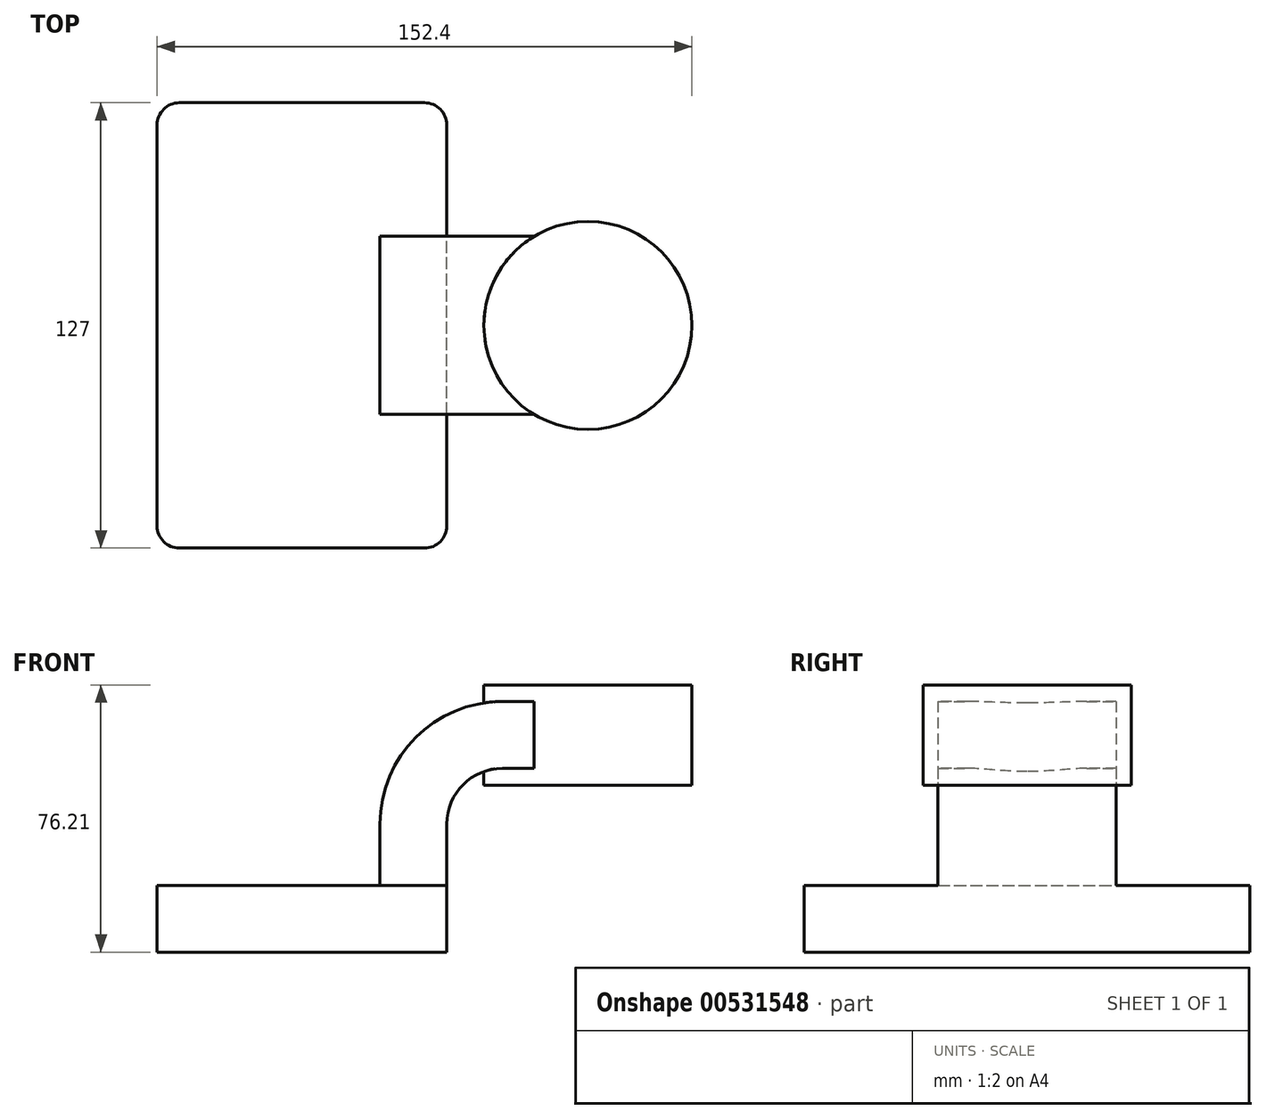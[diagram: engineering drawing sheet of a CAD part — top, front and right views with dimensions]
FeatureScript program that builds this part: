
annotation { "Feature Type Name" : "Feature", "Feature Type Description" : "" }
export const myFeature = defineFeature(function(context is Context, id is Id, definition is map)
    precondition{}
    {
        {
            var Q0;
            Q0=qCreatedBy(makeId("Front.planeOp"),FACE);
            var sketch = newSketch(context, id + "F0", { "sketchPlane" : qUnion([Q0])});
            skLineSegment(sketch, "E0.bottom", {"start": v(-41.28, -9.52) * mm, "end": v(41.28, -9.52) * mm});
            skLineSegment(sketch, "E0.top", {"start": v(-41.28, 9.53) * mm, "end": v(41.28, 9.53) * mm});
            skLineSegment(sketch, "E0.left", {"start": v(-41.28, -9.52) * mm, "end": v(-41.28, 9.53) * mm});
            skLineSegment(sketch, "E0.right", {"start": v(41.28, -9.53) * mm, "end": v(41.28, 9.52) * mm});
            skPoint(sketch, "E0.middle", {"position": v(0, 0) * mm});
            skLineSegment(sketch, "E1.bottom", {"start": v(60.32, 66.68) * mm, "end": v(111.13, 66.68) * mm});
            skLineSegment(sketch, "E1.top", {"start": v(60.32, 38.1) * mm, "end": v(111.13, 38.1) * mm});
            skLineSegment(sketch, "E1.left", {"start": v(60.32, 66.68) * mm, "end": v(60.32, 38.1) * mm});
            skLineSegment(sketch, "E1.right", {"start": v(111.13, 66.68) * mm, "end": v(111.13, 38.1) * mm});
            skPoint(sketch, "E1.middle", {"position": v(85.72, 52.39) * mm});
            skLineSegment(sketch, "E2", {"start": v(41.28, 9.53) * mm, "end": v(41.28, 27) * mm});
            skArc(sketch, "E3", {"start": v(41.28, 27) * mm, "mid": v(45.92, 38.23) * mm, "end": v(57.15, 42.88) * mm});
            skLineSegment(sketch, "E4", {"start": v(57.15, 42.88) * mm, "end": v(81.48, 42.88) * mm});
            skLineSegment(sketch, "E5.0", {"start": v(57.15, 61.93) * mm, "end": v(81.48, 61.93) * mm});
            skArc(sketch, "E5.1", {"start": v(22.23, 27) * mm, "mid": v(32.45, 51.7) * mm, "end": v(57.15, 61.93) * mm});
            skLineSegment(sketch, "E5.2", {"start": v(22.23, 9.52) * mm, "end": v(22.22, 27) * mm});
            skLineSegment(sketch, "E6", {"start": v(81.48, 38.1) * mm, "end": v(81.48, 66.68) * mm});
            skFitSpline(sketch, "E7", {"points": [v(-41.28, 9.53) * mm, v(57.15, 61.93) * mm], "startDerivative": vector(41.68, 78.65) * mm, "endDerivative": vector(125.38, -1.15) * mm});
            skSolve(sketch);
        }
        {
            var Q0;
            Q0=qCreatedBy(makeId("Front.planeOp"),FACE);
            var sketch = newSketch(context, id + "F1", { "sketchPlane" : qUnion([Q0])});
            skLineSegment(sketch, "E8.bottom", {"start": v(-41.28, -9.53) * mm, "end": v(41.28, -9.53) * mm});
            skLineSegment(sketch, "E8.top", {"start": v(-41.28, 9.52) * mm, "end": v(41.28, 9.52) * mm});
            skLineSegment(sketch, "E8.left", {"start": v(-41.28, -9.53) * mm, "end": v(-41.28, 9.52) * mm});
            skLineSegment(sketch, "E8.right", {"start": v(41.28, -9.53) * mm, "end": v(41.28, 9.52) * mm});
            skPoint(sketch, "E8.middle", {"position": v(0, 0) * mm});
            skLineSegment(sketch, "E9.bottom", {"start": v(67.76, 64.92) * mm, "end": v(118.56, 64.92) * mm});
            skLineSegment(sketch, "E9.top", {"start": v(67.76, 36.35) * mm, "end": v(118.56, 36.35) * mm});
            skLineSegment(sketch, "E9.left", {"start": v(67.76, 64.92) * mm, "end": v(67.76, 36.35) * mm});
            skLineSegment(sketch, "E9.right", {"start": v(118.56, 64.92) * mm, "end": v(118.56, 36.35) * mm});
            skPoint(sketch, "E9.middle", {"position": v(93.16, 50.63) * mm});
            skLineSegment(sketch, "E10", {"start": v(41.27, 9.52) * mm, "end": v(41.27, 33.9) * mm});
            skArc(sketch, "E11", {"start": v(41.27, 33.9) * mm, "mid": v(45.92, 45.13) * mm, "end": v(57.15, 49.78) * mm});
            skLineSegment(sketch, "E12", {"start": v(57.15, 49.78) * mm, "end": v(88.25, 49.78) * mm});
            skSolve(sketch);
        }
        {
            var Q0;
            Q0=makeQuery(id+"F1.imprint","IMPRINT",FACE,{"disambiguationData":[TD([[makeQuery(id+"F1.imprint","IMPRINT",EDGE,{"derivedFrom":sQuery(id+"F1.wireOp",EDGE,"E8.bottom")}),1.0]])]});
            extrude(context, id + "F2", {"entities" : qUnion([Q0]), "endBound" : BoundingType.SYMMETRIC, "depth" : 127 * mm, "offsetDistance" : 25.4 * mm});
        }
        {
            var Q0;
            {var subQ1=sQuery(id+"F0.wireOp",EDGE,"E2");Q0=makeQuery(id+"F0.imprint","IMPRINT",FACE,{"disambiguationData":[TD([[makeQuery(id+"F0.imprint","IMPRINT",EDGE,{"derivedFrom":subQ1}),1.0]])]});}
            var Q1;
            {var subQ0=sQuery(id+"F0.wireOp",EDGE,"E5.0");var subQ1=sQuery(id+"F0.wireOp",EDGE,"E1.left");var subQ2=makeQuery(id+"F0.imprint","INTERSECT",VERTEX,{"derivedFrom":[subQ1,subQ0]});Q1=makeQuery(id+"F0.imprint","IMPRINT",FACE,{"disambiguationData":[TD([[makeQuery(id+"F0.imprint","IMPRINT",EDGE,{"disambiguationData":[TD([[subQ2,-1.0]])],"derivedFrom":subQ1}),1.0]])]});}
            extrude(context, id + "F3", {"entities" : qUnion([Q0, Q1]), "operationType" : NewBodyOperationType.ADD, "endBound" : BoundingType.SYMMETRIC, "depth" : 50.8 * mm, "offsetDistance" : 25.4 * mm});
        }
        {
            var Q0;
            Q0=makeQuery(id+"F0.imprint","IMPRINT",FACE,{"disambiguationData":[TD([[makeQuery(id+"F0.imprint","IMPRINT",EDGE,{"derivedFrom":sQuery(id+"F0.wireOp",EDGE,"E5.1")}),1.0]])]});
            extrude(context, id + "F4", {"entities" : qUnion([Q0]), "operationType" : NewBodyOperationType.ADD, "endBound" : BoundingType.SYMMETRIC, "depth" : 15.88 * mm, "offsetDistance" : 25.4 * mm});
        }
        {
            var Q0;
            {var subQ0=sQuery(id+"F0.wireOp",EDGE,"E1.right");Q0=makeQuery(id+"F0.imprint","IMPRINT",FACE,{"disambiguationData":[TD([[makeQuery(id+"F0.imprint","IMPRINT",EDGE,{"derivedFrom":subQ0}),-1.0]])]});}
            var Q1;
            Q1=sQuery(id+"F0.wireOp",EDGE,"E6");
            revolve(context, id + "F5", {"operationType" : NewBodyOperationType.ADD, "entities" : qUnion([Q0]), "axis" : qUnion([Q1]), "revolveType" : RevolveType.FULL});
        }
        {
            var Q0;
            Q0=makeQuery(id+"F2.opExtrude","CAP_EDGE",EDGE,{"disambiguationData":[OSD([sQuery(id+"F1.wireOp",EDGE,"E8.right")])],"isStart":false});
            var Q1;
            Q1=makeQuery(id+"F2.opExtrude","CAP_EDGE",EDGE,{"disambiguationData":[OSD([sQuery(id+"F1.wireOp",EDGE,"E8.left")])],"isStart":false});
            var Q2;
            Q2=makeQuery(id+"F2.opExtrude","CAP_EDGE",EDGE,{"disambiguationData":[OSD([sQuery(id+"F1.wireOp",EDGE,"E8.right")])],"isStart":true});
            fillet(context, id + "F6", {"entities" : qUnion([Q0, Q1, Q2]), "radius" : 6.35 * mm, "tangentPropagation" : true, "allowEdgeOverflow" : false});
        }
        {
            var Q0;
            Q0=makeQuery(id+"F2.opExtrude","CAP_EDGE",EDGE,{"disambiguationData":[OSD([sQuery(id+"F1.wireOp",EDGE,"E8.left")])],"isStart":true});
            fillet(context, id + "F7", {"entities" : qUnion([Q0]), "radius" : 6.35 * mm, "tangentPropagation" : true, "allowEdgeOverflow" : false});
        }
    });
